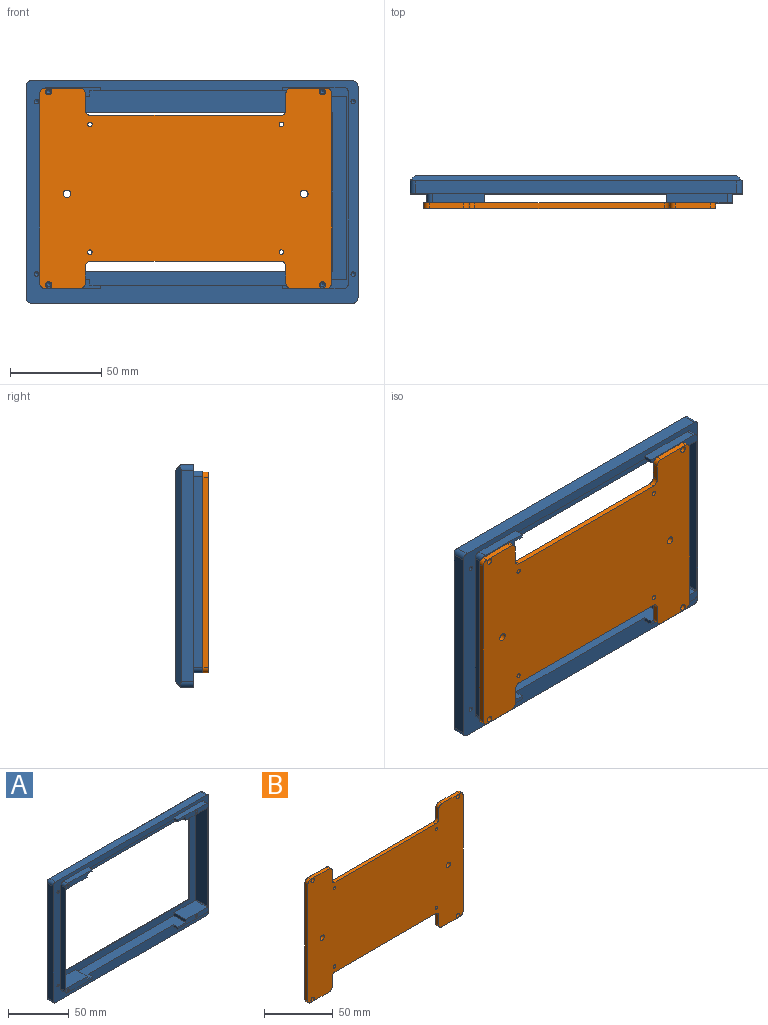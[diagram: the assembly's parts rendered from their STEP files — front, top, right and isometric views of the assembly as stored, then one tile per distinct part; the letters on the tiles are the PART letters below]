
ASSEMBLY  parts=2 mates=1
PART A: 79 faces, bbox 182x15x122 mm
  f0: plane 110.5x36.05mm, normal (0,-1,0), area 402mm2, adj f16,f17,f18,f20,f22,f23,f26,f28
  f1: plane 110.5x31.61mm, normal (0,-1,0), area 348.1mm2, adj f2,f3,f4,f5,f15,f21,f25,f27
  f2: plane 24.5x14mm, normal (0,0,-1), area 343mm2, adj f1,f24,f34,f63
  f3: plane 24.5x14mm, normal (0,0,1), area 343mm2, adj f1,f24,f31,f64
  f4: plane 28.61x5mm, normal (0,0,1), area 143mm2, adj f1,f19,f25,f59
  f5: plane 28.61x5mm, normal (0,0,-1), area 143mm2, adj f1,f19,f27,f62
  f6: plane 153x0.5mm, normal (0,0,-1), area 76.5mm2, adj f24,f67,f70,f71
  f7: plane 86x0.5mm, normal (1,0,0), area 43mm2, adj f24,f67,f68,f74
  f8: plane 153x0.5mm, normal (0,0,1), area 76.5mm2, adj f24,f68,f69,f78
  f9: plane 86x0.5mm, normal (-1,0,0), area 43mm2, adj f24,f69,f70,f75
  f10: plane 176x116mm, normal (0,1,0), area 6776.9mm2, adj f51,f52,f53,f54,f71,f72,f73,f74
  f11: plane 176x7mm, normal (0,0,-1), area 1232mm2, adj f19,f54,f57,f58
  f12: plane 116x7mm, normal (1,0,0), area 812mm2, adj f19,f52,f55,f58
  f13: plane 176x7mm, normal (0,0,1), area 1232mm2, adj f19,f51,f55,f56
  f14: plane 116x7mm, normal (-1,0,0), area 812mm2, adj f19,f53,f56,f57
  f15: plane 104.5x5mm, normal (-1,0,0), area 522.5mm2, adj f1,f19,f59,f62
  f16: plane 33.05x5mm, normal (0,0,1), area 165.2mm2, adj f0,f19,f26,f60
  f17: plane 104.5x5mm, normal (1,0,0), area 522.5mm2, adj f0,f19,f60,f61
  f18: plane 33.05x5mm, normal (0,0,-1), area 165.2mm2, adj f0,f19,f28,f61
  f19: plane 182x122mm, normal (0,-1,0), area 4064.3mm2, adj f4,f5,f11,f12,f13,f14,f15,f16
  f20: plane 25.2x14mm, normal (0,0,-1), area 352.8mm2, adj f0,f24,f33,f66
  f21: plane 99.5x14mm, normal (1,0,0), area 1393mm2, adj f1,f24,f63,f64
  f22: plane 25.2x14mm, normal (0,0,1), area 352.8mm2, adj f0,f24,f30,f65
  f23: plane 99.5x14mm, normal (-1,0,0), area 1393mm2, adj f0,f24,f65,f66
  f24: plane 165.7x106.5mm, normal (0,-1,0), area 3944.9mm2, adj f2,f3,f6,f7,f8,f9,f20,f21
  f25: plane 5x2mm, normal (1,0,0), area 10mm2, adj f1,f4,f19,f32
  f26: plane 5x2mm, normal (-1,0,0), area 10mm2, adj f0,f16,f19,f32
  f27: plane 5x2mm, normal (1,0,0), area 10mm2, adj f1,f5,f19,f29
  f28: plane 5x2mm, normal (-1,0,0), area 10mm2, adj f0,f18,f19,f29
  f29: plane 115x14mm, normal (0,0,1), area 1110.3mm2, adj f0,f1,f19,f24,f27,f28,f30,f31
  f30: plane 14x3mm, normal (-1,0,0), area 42mm2, adj f0,f22,f24,f29
  f31: plane 14x3mm, normal (1,0,0), area 42mm2, adj f1,f3,f24,f29
  f32: plane 115x14mm, normal (0,0,-1), area 1110.3mm2, adj f0,f1,f19,f24,f25,f26,f33,f34
  f33: plane 14x3mm, normal (-1,0,0), area 42mm2, adj f0,f20,f24,f32
  f34: plane 14x3mm, normal (1,0,0), area 42mm2, adj f1,f2,f24,f32
  f35: cone r=0mm half-angle=59deg, axis (0,-1,0), area 5.7mm2, adj f36
  f36: cylinder r=1.25mm len=8mm, axis (0,-1,0), area 62.8mm2, adj f1,f35
  f37: cone r=0mm half-angle=59deg, axis (0,-1,0), area 5.7mm2, adj f38
  f38: cylinder r=1.25mm len=8mm, axis (0,-1,0), area 62.8mm2, adj f1,f37
  f39: cone r=0mm half-angle=59deg, axis (0,-1,0), area 5.7mm2, adj f40
  f40: cylinder r=1.25mm len=8mm, axis (0,-1,0), area 62.8mm2, adj f0,f39
  f41: cone r=0mm half-angle=59deg, axis (0,-1,0), area 5.7mm2, adj f42
  f42: cylinder r=1.25mm len=8mm, axis (0,-1,0), area 62.8mm2, adj f0,f41
  f43: cone r=0mm half-angle=59deg, axis (0,-1,0), area 5.7mm2, adj f44
  f44: cylinder r=1.25mm len=8mm, axis (0,-1,0), area 62.8mm2, adj f19,f43
  f45: cone r=0mm half-angle=59deg, axis (0,-1,0), area 5.7mm2, adj f46
  f46: cylinder r=1.25mm len=8mm, axis (0,-1,0), area 62.8mm2, adj f19,f45
  f47: cone r=0mm half-angle=59deg, axis (0,-1,0), area 5.7mm2, adj f48
  f48: cylinder r=1.25mm len=8mm, axis (0,-1,0), area 62.8mm2, adj f19,f47
  f49: cone r=0mm half-angle=59deg, axis (0,-1,0), area 5.7mm2, adj f50
  f50: cylinder r=1.25mm len=8mm, axis (0,-1,0), area 62.8mm2, adj f19,f49
  f51: plane 180.24x3mm, normal (0,0.71,0.71), area 756.7mm2, adj f10,f13,f52,f53,f55,f56
  f52: plane 120.24x3mm, normal (0.71,0.71,0), area 502.1mm2, adj f10,f12,f51,f54,f55,f58
  f53: plane 120.24x3mm, normal (-0.71,0.71,0), area 502.1mm2, adj f10,f14,f51,f54,f56,f57
  f54: plane 180.24x3mm, normal (0,0.71,-0.71), area 756.7mm2, adj f10,f11,f52,f53,f57,f58
  f55: cylinder r=3mm len=7.88mm, axis (0,-1,0), area 34.4mm2, adj f12,f13,f19,f51,f52
  f56: cylinder r=3mm len=7.88mm, axis (0,1,0), area 34.4mm2, adj f13,f14,f19,f51,f53
  f57: cylinder r=3mm len=7.88mm, axis (0,-1,0), area 34.4mm2, adj f11,f14,f19,f53,f54
  f58: cylinder r=3mm len=7.88mm, axis (0,1,0), area 34.4mm2, adj f11,f12,f19,f52,f54
  f59: cylinder r=3mm len=5mm, axis (0,1,0), area 23.6mm2, adj f1,f4,f15,f19
  f60: cylinder r=3mm len=5mm, axis (0,-1,0), area 23.6mm2, adj f0,f16,f17,f19
  f61: cylinder r=3mm len=5mm, axis (0,1,0), area 23.6mm2, adj f0,f17,f18,f19
  f62: cylinder r=3mm len=5mm, axis (0,-1,0), area 23.6mm2, adj f1,f5,f15,f19
  f63: cylinder r=0.5mm len=14mm, axis (0,-1,0), area 11mm2, adj f1,f2,f21,f24
  f64: cylinder r=0.5mm len=14mm, axis (0,1,0), area 11mm2, adj f1,f3,f21,f24
  f65: cylinder r=0.5mm len=14mm, axis (0,-1,0), area 11mm2, adj f0,f22,f23,f24
  f66: cylinder r=0.5mm len=14mm, axis (0,1,0), area 11mm2, adj f0,f20,f23,f24
  f67: cylinder r=0.5mm len=0.5mm, axis (0,-1,0), area 0.4mm2, adj f6,f7,f24,f72
  f68: cylinder r=0.5mm len=0.5mm, axis (0,1,0), area 0.4mm2, adj f7,f8,f24,f76
  f69: cylinder r=0.5mm len=0.5mm, axis (0,-1,0), area 0.4mm2, adj f8,f9,f24,f77
  f70: cylinder r=0.5mm len=0.5mm, axis (0,1,0), area 0.4mm2, adj f6,f9,f24,f73
  f71: plane 153x0.5mm, normal (0,0.71,-0.71), area 108.2mm2, adj f6,f10,f72,f73
  f72: cone r=1mm half-angle=45deg, axis (0,1,0), area 0.8mm2, adj f10,f67,f71,f74
  f73: cone r=1mm half-angle=45deg, axis (0,1,0), area 0.8mm2, adj f10,f70,f71,f75
  f74: plane 86x0.5mm, normal (0.71,0.71,0), area 60.8mm2, adj f7,f10,f72,f76
  f75: plane 86x0.5mm, normal (-0.71,0.71,0), area 60.8mm2, adj f9,f10,f73,f77
  f76: cone r=1mm half-angle=45deg, axis (0,1,0), area 0.8mm2, adj f10,f68,f74,f78
  f77: cone r=1mm half-angle=45deg, axis (0,1,0), area 0.8mm2, adj f10,f69,f75,f78
  f78: plane 153x0.5mm, normal (0,0.71,0.71), area 108.2mm2, adj f8,f10,f76,f77
PART B: 36 faces, bbox 160x3x110 mm
  f0: plane 19x3mm, normal (0,0,-1), area 57mm2, adj f2,f3,f24,f35
  f1: plane 19x3mm, normal (0,0,1), area 57mm2, adj f2,f3,f31,f34
  f2: plane 160x110mm, normal (0,-1,0), area 14206.4mm2, adj f0,f1,f4,f5,f6,f7,f8,f9
  f3: plane 160x110mm, normal (0,1,0), area 14206.4mm2, adj f0,f1,f4,f5,f6,f7,f8,f9
  f4: plane 19x3mm, normal (0,0,-1), area 57mm2, adj f2,f3,f25,f32
  f5: plane 104x3mm, normal (1,0,0), area 312mm2, adj f2,f3,f32,f33
  f6: plane 19x3mm, normal (0,0,1), area 57mm2, adj f2,f3,f28,f33
  f7: plane 104x3mm, normal (-1,0,0), area 312mm2, adj f2,f3,f34,f35
  f8: plane 9x3mm, normal (1,0,0), area 27mm2, adj f2,f3,f24,f27
  f9: plane 9x3mm, normal (-1,0,0), area 27mm2, adj f2,f3,f25,f26
  f10: plane 104x3mm, normal (0,0,-1), area 312mm2, adj f2,f3,f26,f27
  f11: plane 9x3mm, normal (1,0,0), area 27mm2, adj f2,f3,f30,f31
  f12: plane 104x3mm, normal (0,0,1), area 312mm2, adj f2,f3,f29,f30
  f13: plane 9x3mm, normal (-1,0,0), area 27mm2, adj f2,f3,f28,f29
  f14: cylinder r=1.75mm len=3.5mm, axis (0,-1,0), area 33mm2, adj f2,f3
  f15: cylinder r=1.75mm len=3.5mm, axis (0,-1,0), area 33mm2, adj f2,f3
  f16: cylinder r=1.75mm len=3.5mm, axis (0,-1,0), area 33mm2, adj f2,f3
  f17: cylinder r=1.75mm len=3.5mm, axis (0,-1,0), area 33mm2, adj f2,f3
  f18: cylinder r=1.25mm len=3mm, axis (0,-1,0), area 23.6mm2, adj f2,f3
  f19: cylinder r=1.25mm len=3mm, axis (0,-1,0), area 23.6mm2, adj f2,f3
  f20: cylinder r=1.25mm len=3mm, axis (0,-1,0), area 23.6mm2, adj f2,f3
  f21: cylinder r=1.25mm len=3mm, axis (0,-1,0), area 23.6mm2, adj f2,f3
  f22: cylinder r=2.1mm len=4.2mm, axis (0,-1,0), area 39.6mm2, adj f2,f3
  f23: cylinder r=2.1mm len=4.2mm, axis (0,-1,0), area 39.6mm2, adj f2,f3
  f24: cylinder r=3mm len=3mm, axis (0,-1,0), area 14.1mm2, adj f0,f2,f3,f8
  f25: cylinder r=3mm len=3mm, axis (0,1,0), area 14.1mm2, adj f2,f3,f4,f9
  f26: cylinder r=3mm len=3mm, axis (0,-1,0), area 14.1mm2, adj f2,f3,f9,f10
  f27: cylinder r=3mm len=3mm, axis (0,1,0), area 14.1mm2, adj f2,f3,f8,f10
  f28: cylinder r=3mm len=3mm, axis (0,1,0), area 14.1mm2, adj f2,f3,f6,f13
  f29: cylinder r=3mm len=3mm, axis (0,-1,0), area 14.1mm2, adj f2,f3,f12,f13
  f30: cylinder r=3mm len=3mm, axis (0,1,0), area 14.1mm2, adj f2,f3,f11,f12
  f31: cylinder r=3mm len=3mm, axis (0,-1,0), area 14.1mm2, adj f1,f2,f3,f11
  f32: cylinder r=3mm len=3mm, axis (0,-1,0), area 14.1mm2, adj f2,f3,f4,f5
  f33: cylinder r=3mm len=3mm, axis (0,1,0), area 14.1mm2, adj f2,f3,f5,f6
  f34: cylinder r=3mm len=3mm, axis (0,-1,0), area 14.1mm2, adj f1,f2,f3,f7
  f35: cylinder r=3mm len=3mm, axis (0,1,0), area 14.1mm2, adj f0,f2,f3,f7
PLACE A t=(0.27,-7.34,0.01)mm
PLACE B rot(axis=(0,0,1),180deg) t=(-3.23,-10.34,2.01)mm
MATE fastened B.f14 <-> A.f41  axis (0,1,0) through (71.77,-7.34,55.01)mm
